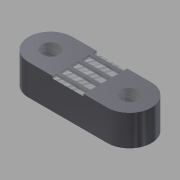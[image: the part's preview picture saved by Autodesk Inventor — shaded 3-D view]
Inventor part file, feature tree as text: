
AUTODESK INVENTOR PART (.ipt)
format: ipt  version: 2011 SP2 (Build 150309200, 309)  size: 131,072 bytes
history: native  units: mm
features: sketch x3, extrude x2, hole x1
ambient origin geometry x8: Origin, YZ Plane, XZ Plane, XY Plane, X Axis, Y Axis, Z Axis, Center Point
bodies: Solid1 (feature_tree)
feature tree (6):
  extrude  "Extrusion1"  Depth=18.0mm
  hole  "Hole1"  [1 undecoded]
  extrude  "Extrusion2"  Depth=0.7mm
  sketch  "Sketch1"  dims[d0=5.0mm d1=18.0mm]
  sketch  "Sketch2"  dims[d2=7.0mm d3=0.0mm]
  sketch  "Sketch3"  dims[d4=4.0mm d5=6.0mm d6=4.0mm d7=2.0mm d8=90.0deg d9=8.0mm d10=20.594885mm d11=7.0mm d12=0.7mm d13=1.8mm d14=0.5mm d15=0.0mm]
note: 1 required parameter value undecoded (feature->parameter linkage not recoverable at this tier; creation-order binding heuristic only, values carry confidence <= 0.55)
